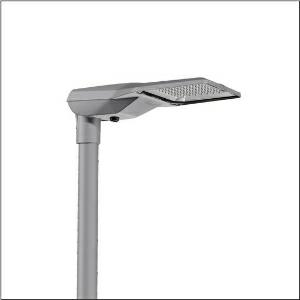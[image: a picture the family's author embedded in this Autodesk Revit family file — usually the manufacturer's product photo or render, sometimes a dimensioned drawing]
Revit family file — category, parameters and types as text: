
# Revit family: streetlight_sl_21_midi___p0_8a_5xe3u33r08nb_1bfe
name_source: partatom
category: Lighting Fixtures
units: mm (PartAtom-declared; Revit-internal decimal feet)

## family parameters
Cut with Voids When Loaded = No
Host = Face
Light Source = No
Part Type = Normal
Room Calculation Point = No
Round Connector Dimension = Use Diameter
Shared = No

## types (1)
- --- (1 x LED, 22900 lm, 151.2 W, 3000K)
    Apparent Load = 151 VA
    CIE Flux Codes = 36 69 97 100 100
    Color Rendering = 70
    Color Temperature = 3000K
    Default Elevation = 1800 mm
    Description = Streetlight SL 21 midi, mast luminaire, primary light control with lens, of PMMA, primary optical cover: cover, of toughened safety glass, transparent, light distribution: P0.8a, light emission: direct distribution, primary light characteristic: asymmetric, installation type: post-top, side-entry, LED, High Power LED, rated luminous flux: 22.900lm, luminous efficacy: 152lm/W, light colour: 730, colour temperature: 3000K, control gear: D4i, control: pre-setting: logarithmic dimming characteristic, flexible luminous flux parameterisation, time-dependent luminous flux control, constant luminous flux control, overheat protection, mains connection: 230..240V, AC, 50/60Hz, start of lifetime: 151W, end of service life: 157W, reduction: 70W, luminaire housing, of diecast aluminium, powder-coated, Siteco® metallic grey (DB 702S), corrosivity category C5 mid according to DIN EN ISO 12944, multi-level sealing system, sealing non-destructively replaceable, inclination adjustable: 0°, 5°, 10°, 15°, please order mast flange separately, length: 644mm, width: 335mm, height: 110mm, mast flange for spigot size: 42mm (side-entry): 5XC10008XM4, 60/48mm (side-entry/post-top): 5XC10108XM2, 76/60mm (side-entry/post-top): 5XC10108XM1, mounting height: 4..8m, Smart Interface below, protection rating (complete): IP66, insulation class (complete): insulation class II (safety insulation), certification: CE, ENEC, ENEC+, VDE, impact resistance: IK10, permissible operating ambient temperature for outdoor applications: -40..+50°C, standard-compliant lighting for roads and squares, packaging unit: 1 piece

Light Distribution: P0.8a
    Height = 111 mm
    Lamp = 1 x LED
    Lamp Light Flux = 22900 lm
    Lamp Power = 151.2 W
    Lamp count = 1
    Length = 644 mm
    Luminous efficacy = 151 lm/W
    Manufacturer = Siteco
    ModVariant = No
    Model = 5XE3U33R08NB
    Number of Poles = 1
    OnlyDefault = Yes
    Power Factor = 1
    Product Name = Streetlight SL 21 midi | P0.8a
    Product group = mast luminaire | pylon top
    ProductGroupID = 6100
    Protection Class = Protection class II
    Protection Degree = IP 66
    RLX_Detail_Level = 1
    RLX_Emergency_Light_Flux = 0 lm
    RLX_Emergency_Type = 0
    RLX_Emergency_Type_DB = No
    RlxData = <blob elided: 90317 chars, md5=896d3e43>
    Socket = socket
    Standby Power = 0 W
    System Light Flux = 22901 lm
    System Power = 151 W
    Type Comments = factory setting: luminous flux: 100 % | dim-lin: 254 | 802 mA
    Type Image = l_1004300.jpg
    URL = http://relux.com
    VarID = @adj_093001
    Voltage = 0 V
    Weight = 0.00 kg
    Width = 336 mm

## geometry (parser evidence)
native form markers: Blend x4, Sweep x10
no freeform markers — native parametric forms only
